# Revit family: NAU_Naughtone_Stng_Fiji_Sofa1
name_source: partatom
category: Furniture
revit_build: Autodesk Revit 2015 (Build: 20140903_1530(x64)
units: mm (PartAtom-declared; Revit-internal decimal feet)

## types (2) — shared parameters
Assembly Code = E2020200
AssetType = Movable
BIMObjectName = NAU_Naughtone_Seating_Fiji_Sofa
Category = Pr_40_50_12_81 : Sofas
Color = Various
DurationUnit = year
Finish = Upholstered
IfcExportAs = IfcFurnishingElementType
IfcExportType = SOFA
Keynote = Pr_40_50_12_81
MainColor = Various
ManufacturerAddress = "Knaresborough Tech Park, Manse Lane, Knaresborough, HG5 8LF"
ManufacturerName = Naughtone
ManufacturerURL = www.naughtone.com
Material = Fabric, plywood frame, foam
NBSDescription = Seating
NBSReference = 45-35-72/352
Name = Seating_Fiji_Sofa_Naughtone
NominalHeight = 885 mm
NominalWidth = 865 mm  [stored 2.83793 ft]
ProductInformation = www.naughtone.com/products/fiji/
Shape = Rectangular
SustainabilityPerformance = FSC certifeied, SCS indoor advantage gold
URL = www.naughtone.com
Uniclass2015Code = Pr_40_50_12_81
Uniclass2015Title = Sofas
Uniclass2015Version = Products v1.13
Version = 1
WarrantyDescription = Request warranty information from naughtone
WarrantyDurationLabor = 5
WarrantyDurationParts = 5
WarrantyDurationUnit = year

## per-type parameters (varying)
| type | CushionOffset | Description | Is3Seater | Model | ModelNumber | ModelReference | NominalLength | Size |
| Fiji 2 Seat Sofa | 0 mm  [stored 0 ft] | Fiji 2 seat sofa luxuriously upholstered sofa | No | FIJI2SF | FIJI2SF | Fiji 2 seat sofa luxuriously upholstered sofa | 1650 mm  [stored 5.41339 ft] | 1650 x 865 x 885mm |
| Fiji 3 Seat Sofa | 338 mm | Fiji 3 seat sofa luxuriously upholstered sofa | Yes | FIJI3SF | FIJI3SF | Fiji 3 seat sofa luxuriously upholstered sofa | 2250 mm | 2250 x 865 x 885mm |

note: [stored X ft] marks values corroborated as IEEE doubles in the binary element streams (Revit-internal decimal feet)

## geometry (parser evidence)
native form markers: Sweep x6
no freeform markers — native parametric forms only
